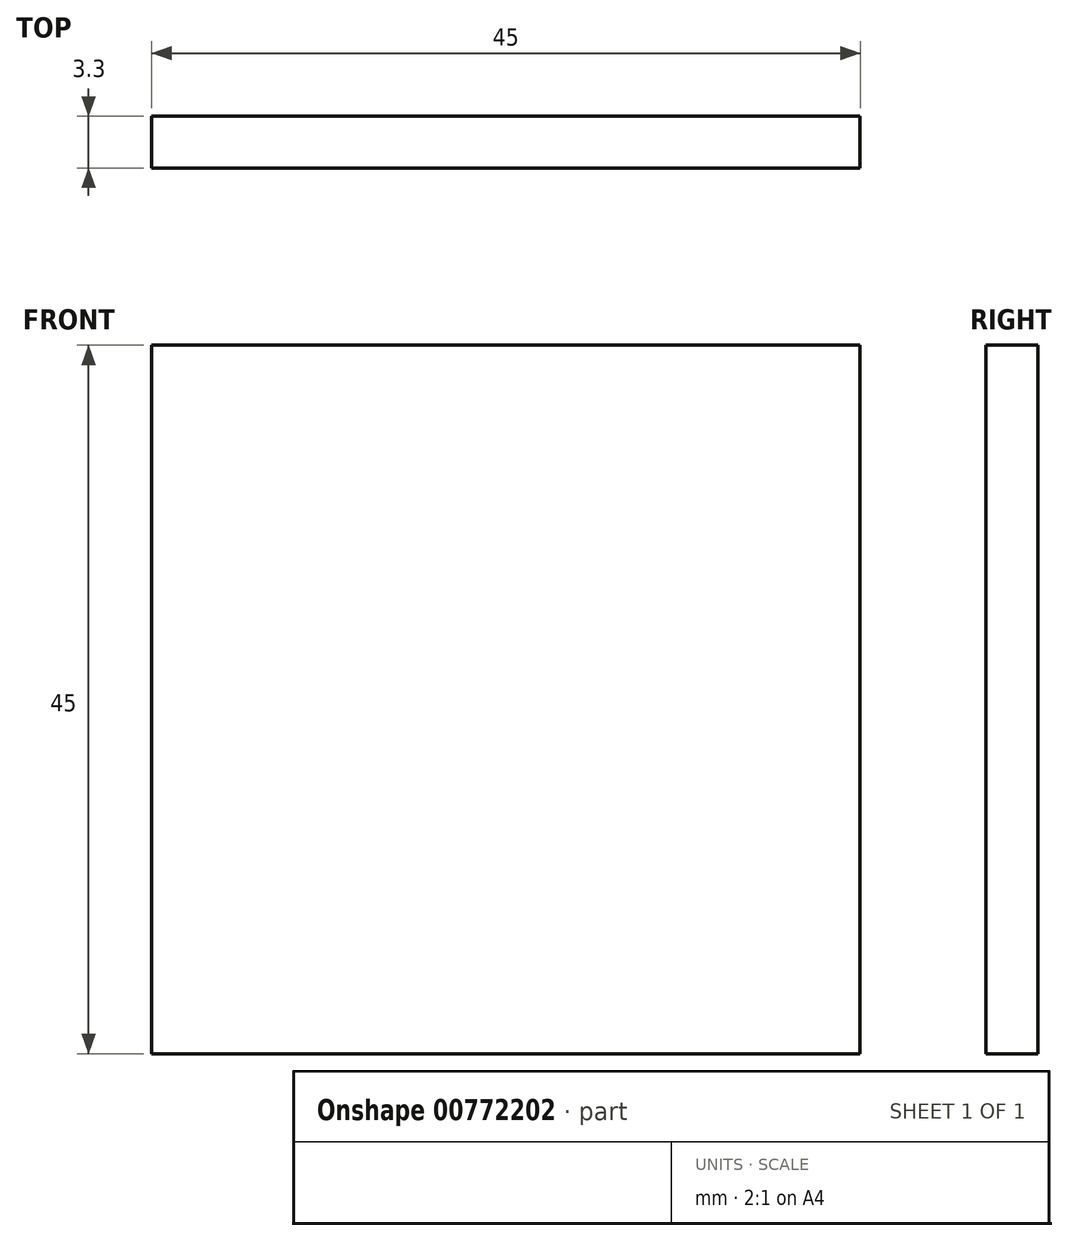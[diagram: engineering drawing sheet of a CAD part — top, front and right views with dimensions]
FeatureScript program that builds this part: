
annotation { "Feature Type Name" : "Feature", "Feature Type Description" : "" }
export const myFeature = defineFeature(function(context is Context, id is Id, definition is map)
    precondition{}
    {
        {
            var Q0;
            Q0=qCreatedBy(makeId("Front.planeOp"),FACE);
            var sketch = newSketch(context, id + "F0", { "sketchPlane" : qUnion([Q0])});
            skLineSegment(sketch, "E0.bottom", {"start": v(-10.27, 2.39) * mm, "end": v(34.73, 2.39) * mm});
            skLineSegment(sketch, "E0.top", {"start": v(-10.27, -42.61) * mm, "end": v(34.73, -42.61) * mm});
            skLineSegment(sketch, "E0.left", {"start": v(-10.27, 2.39) * mm, "end": v(-10.27, -42.61) * mm});
            skLineSegment(sketch, "E0.right", {"start": v(34.73, 2.39) * mm, "end": v(34.73, -42.61) * mm});
            skSolve(sketch);
        }
        {
            var Q0;
            Q0 = qSketchRegion(id + "F0", true);
            extrude(context, id + "F1", {"entities" : qUnion([Q0]), "depth" : 3.3 * mm, "offsetDistance" : 25 * mm});
        }
    });
